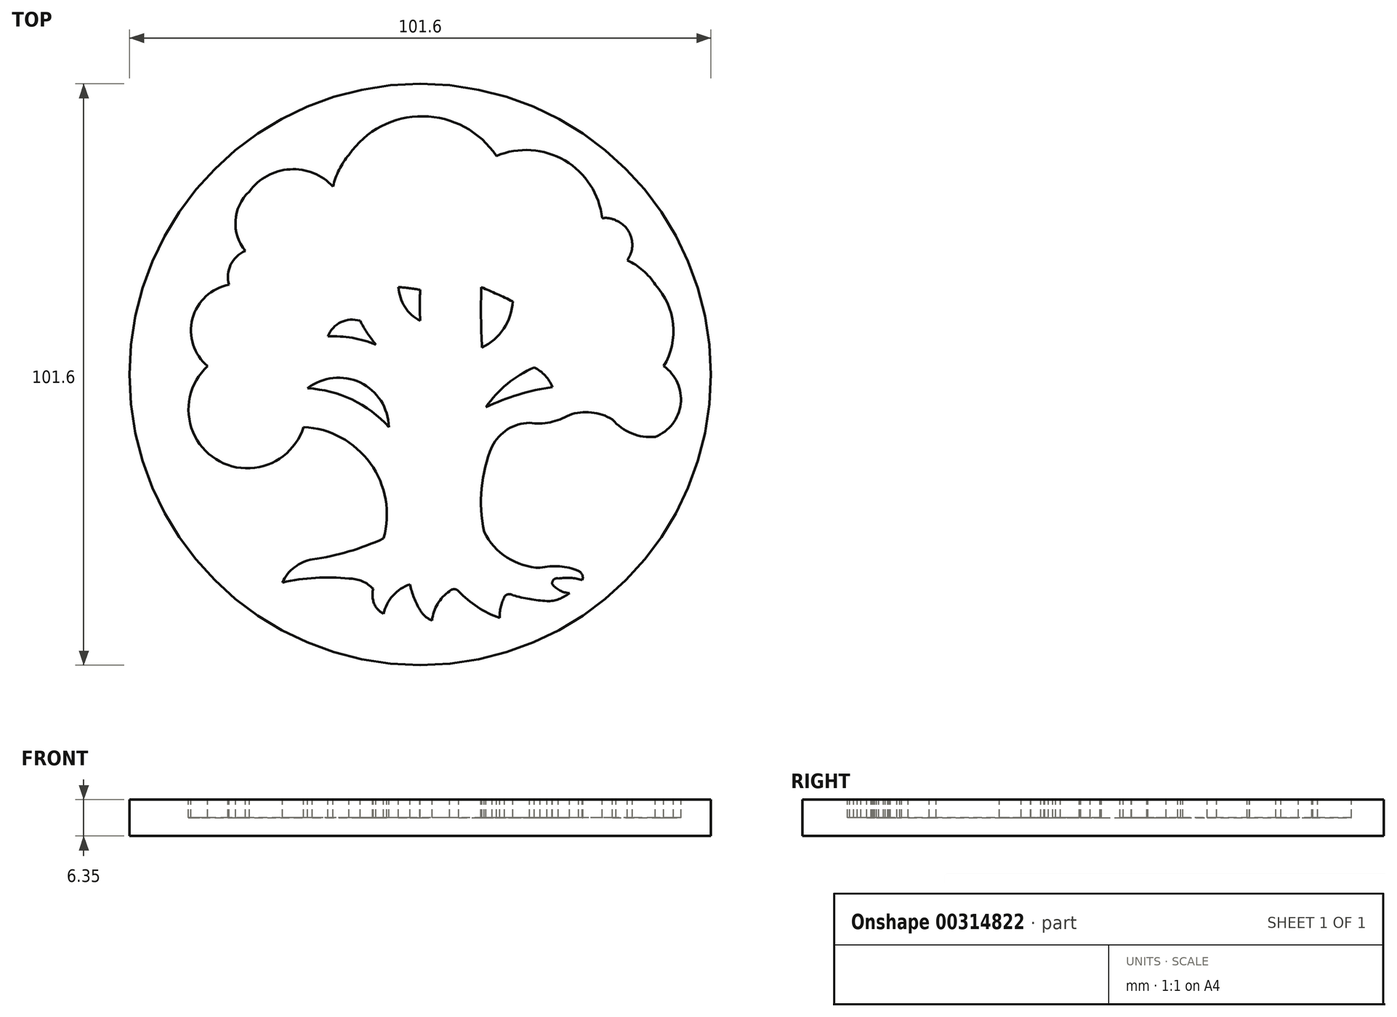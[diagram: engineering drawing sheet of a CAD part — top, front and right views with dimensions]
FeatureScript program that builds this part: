
annotation { "Feature Type Name" : "Feature", "Feature Type Description" : "" }
export const myFeature = defineFeature(function(context is Context, id is Id, definition is map)
    precondition{}
    {
        {
            var Q0;
            Q0=qCreatedBy(makeId("Top.planeOp"),FACE);
            var sketch = newSketch(context, id + "F0", { "sketchPlane" : qUnion([Q0])});
            skCircle(sketch, "E0", {"center": v(0, 0) * mm, "radius": 50.8 * mm});
            skSolve(sketch);
        }
        {
            var Q0;
            Q0 = qSketchRegion(id + "F0", true);
            extrude(context, id + "F1", {"entities" : qUnion([Q0]), "depth" : 6.35 * mm});
        }
        {
            var Q0;
            Q0=makeQuery(id+"F1.opExtrude","CAP_FACE",FACE,{"disambiguationData":[OSD([sQuery(id+"F0.wireOp",EDGE,"E0")])],"isStart":false});
            var sketch = newSketch(context, id + "F2", { "sketchPlane" : qUnion([Q0])});
            skArc(sketch, "E1", {"start": v(-6.4, -28.65) * mm, "mid": v(-8.71, -15.53) * mm, "end": v(-20.4, -9.17) * mm});
            skArc(sketch, "E2", {"start": v(-18.85, -32.3) * mm, "mid": v(-12.5, -30.92) * mm, "end": v(-6.4, -28.65) * mm});
            skArc(sketch, "E3", {"start": v(-18.85, -32.3) * mm, "mid": v(-21.97, -33.68) * mm, "end": v(-24.1, -36.34) * mm});
            skArc(sketch, "E4", {"start": v(-12.46, -35.65) * mm, "mid": v(-18.3, -35.54) * mm, "end": v(-24.1, -36.34) * mm});
            skArc(sketch, "E5", {"start": v(-8.24, -37.47) * mm, "mid": v(-10.16, -36.12) * mm, "end": v(-12.46, -35.65) * mm});
            skArc(sketch, "E6", {"start": v(-8.24, -37.47) * mm, "mid": v(-8.31, -39.07) * mm, "end": v(-7.79, -40.6) * mm});
            skArc(sketch, "E7", {"start": v(-7.79, -40.6) * mm, "mid": v(-7.17, -41.3) * mm, "end": v(-6.4, -41.83) * mm});
            skArc(sketch, "E8", {"start": v(-1.79, -36.67) * mm, "mid": v(-4.78, -38.64) * mm, "end": v(-6.4, -41.83) * mm});
            skArc(sketch, "E9", {"start": v(-1.79, -36.67) * mm, "mid": v(-1.09, -39.01) * mm, "end": v(0, -41.2) * mm});
            skArc(sketch, "E10", {"start": v(0, -41.2) * mm, "mid": v(0.87, -42.27) * mm, "end": v(2.06, -42.97) * mm});
            skArc(sketch, "E11", {"start": v(5.1, -37.87) * mm, "mid": v(3.03, -40.09) * mm, "end": v(2.06, -42.97) * mm});
            skArc(sketch, "E12", {"start": v(6.7, -37.87) * mm, "mid": v(5.9, -37.51) * mm, "end": v(5.1, -37.87) * mm});
            skArc(sketch, "E13", {"start": v(6.7, -37.87) * mm, "mid": v(10.02, -40.63) * mm, "end": v(13.88, -42.54) * mm});
            skArc(sketch, "E14", {"start": v(14.74, -38.8) * mm, "mid": v(14.08, -40.62) * mm, "end": v(13.88, -42.54) * mm});
            skArc(sketch, "E15", {"start": v(16.17, -38.58) * mm, "mid": v(15.4, -38.4) * mm, "end": v(14.74, -38.8) * mm});
            skArc(sketch, "E16", {"start": v(16.17, -38.58) * mm, "mid": v(19.13, -39.23) * mm, "end": v(22.15, -39.6) * mm});
            skArc(sketch, "E17", {"start": v(22.15, -39.6) * mm, "mid": v(24.23, -39.25) * mm, "end": v(26.06, -38.2) * mm});
            skArc(sketch, "E18", {"start": v(23.08, -36.67) * mm, "mid": v(24.4, -37.75) * mm, "end": v(26.06, -38.2) * mm});
            skArc(sketch, "E19", {"start": v(24.13, -35.65) * mm, "mid": v(23.3, -35.85) * mm, "end": v(23.08, -36.67) * mm});
            skArc(sketch, "E20", {"start": v(28.33, -35.91) * mm, "mid": v(26.25, -35.54) * mm, "end": v(24.13, -35.65) * mm});
            skArc(sketch, "E21", {"start": v(28.33, -35.91) * mm, "mid": v(28.3, -34.99) * mm, "end": v(27.66, -34.33) * mm});
            skArc(sketch, "E22", {"start": v(27.66, -34.33) * mm, "mid": v(24.35, -33.53) * mm, "end": v(20.96, -33.79) * mm});
            skArc(sketch, "E23", {"start": v(11.14, -27.47) * mm, "mid": v(15.18, -31.98) * mm, "end": v(20.96, -33.79) * mm});
            skArc(sketch, "E24", {"start": v(12.54, -12.56) * mm, "mid": v(10.7, -19.91) * mm, "end": v(11.14, -27.47) * mm});
            skArc(sketch, "E25", {"start": v(19.1, -8.45) * mm, "mid": v(15.25, -9.6) * mm, "end": v(12.54, -12.56) * mm});
            skArc(sketch, "E26", {"start": v(19.1, -8.45) * mm, "mid": v(22.7, -8.35) * mm, "end": v(26.06, -7.08) * mm});
            skArc(sketch, "E27", {"start": v(33.57, -7.84) * mm, "mid": v(29.9, -6.62) * mm, "end": v(26.06, -7.08) * mm});
            skArc(sketch, "E28", {"start": v(33.57, -7.84) * mm, "mid": v(36.95, -10.3) * mm, "end": v(41.09, -10.89) * mm});
            skArc(sketch, "E29", {"start": v(41.09, -10.89) * mm, "mid": v(45.5, -5.16) * mm, "end": v(42.56, 1.46) * mm});
            skArc(sketch, "E30", {"start": v(42.56, 1.46) * mm, "mid": v(44.19, 8.81) * mm, "end": v(41.09, 15.68) * mm});
            skArc(sketch, "E31", {"start": v(41.09, 15.68) * mm, "mid": v(38.94, 18.17) * mm, "end": v(36.17, 19.95) * mm});
            skArc(sketch, "E32", {"start": v(36.17, 19.95) * mm, "mid": v(36.88, 23.9) * mm, "end": v(34.23, 26.91) * mm});
            skArc(sketch, "E33", {"start": v(34.23, 26.91) * mm, "mid": v(33.04, 27.31) * mm, "end": v(31.78, 27.3) * mm});
            skArc(sketch, "E34", {"start": v(31.78, 27.3) * mm, "mid": v(25.27, 37.39) * mm, "end": v(13.3, 38.2) * mm});
            skArc(sketch, "E35", {"start": v(13.3, 38.2) * mm, "mid": v(0.47, 45.13) * mm, "end": v(-12.46, 38.4) * mm});
            skArc(sketch, "E36", {"start": v(-12.46, 38.4) * mm, "mid": v(-14.18, 35.78) * mm, "end": v(-15.25, 32.84) * mm});
            skArc(sketch, "E37", {"start": v(-15.25, 32.84) * mm, "mid": v(-22.78, 35.86) * mm, "end": v(-29.9, 31.96) * mm});
            skArc(sketch, "E38", {"start": v(-29.9, 31.96) * mm, "mid": v(-32.29, 26.9) * mm, "end": v(-30.57, 21.58) * mm});
            skArc(sketch, "E39", {"start": v(-30.57, 21.58) * mm, "mid": v(-33.14, 19.18) * mm, "end": v(-33.4, 15.68) * mm});
            skArc(sketch, "E40", {"start": v(-33.4, 15.68) * mm, "mid": v(-39.8, 9.76) * mm, "end": v(-37.17, 1.46) * mm});
            skArc(sketch, "E41", {"start": v(-37.17, 1.46) * mm, "mid": v(-35.72, -14.8) * mm, "end": v(-20.4, -9.17) * mm});
            skArc(sketch, "E42", {"start": v(-5.5, -9.17) * mm, "mid": v(-11.92, -4.39) * mm, "end": v(-19.67, -2.4) * mm});
            skArc(sketch, "E43", {"start": v(-5.5, -9.17) * mm, "mid": v(-10.5, -1.4) * mm, "end": v(-19.67, -2.4) * mm});
            skArc(sketch, "E44", {"start": v(-7.79, 5.25) * mm, "mid": v(-11.9, 6.4) * mm, "end": v(-16.15, 6.68) * mm});
            skArc(sketch, "E45", {"start": v(-10.52, 9.39) * mm, "mid": v(-9.26, 7.25) * mm, "end": v(-7.79, 5.25) * mm});
            skArc(sketch, "E46", {"start": v(-10.52, 9.39) * mm, "mid": v(-13.87, 9.14) * mm, "end": v(-16.15, 6.68) * mm});
            skArc(sketch, "E47", {"start": v(-3.8, 15.27) * mm, "mid": v(-2.7, 11.82) * mm, "end": v(0, 9.39) * mm});
            skArc(sketch, "E48", {"start": v(0, 14.79) * mm, "mid": v(-1.9, 15.08) * mm, "end": v(-3.8, 15.27) * mm});
            skArc(sketch, "E49", {"start": v(0, 14.79) * mm, "mid": v(-0.1, 12.09) * mm, "end": v(0, 9.39) * mm});
            skArc(sketch, "E50", {"start": v(10.67, 15.27) * mm, "mid": v(10.62, 9.99) * mm, "end": v(10.8, 4.7) * mm});
            skArc(sketch, "E51", {"start": v(16.17, 12.77) * mm, "mid": v(13.43, 14.05) * mm, "end": v(10.67, 15.27) * mm});
            skArc(sketch, "E52", {"start": v(10.8, 4.7) * mm, "mid": v(14.58, 8) * mm, "end": v(16.17, 12.77) * mm});
            skArc(sketch, "E53", {"start": v(19.91, 1.22) * mm, "mid": v(15.2, -1.64) * mm, "end": v(11.49, -5.71) * mm});
            skArc(sketch, "E54", {"start": v(23.08, -2.19) * mm, "mid": v(21.83, -0.18) * mm, "end": v(19.91, 1.22) * mm});
            skArc(sketch, "E55", {"start": v(23.08, -2.19) * mm, "mid": v(17.15, -3.5) * mm, "end": v(11.49, -5.71) * mm});
            skSolve(sketch);
        }
        {
            var Q0;
            Q0 = qSketchRegion(id + "F2", true);
            extrude(context, id + "F3", {"entities" : qUnion([Q0]), "operationType" : NewBodyOperationType.REMOVE, "oppositeDirection" : true, "depth" : 3.17 * mm});
        }
    });
